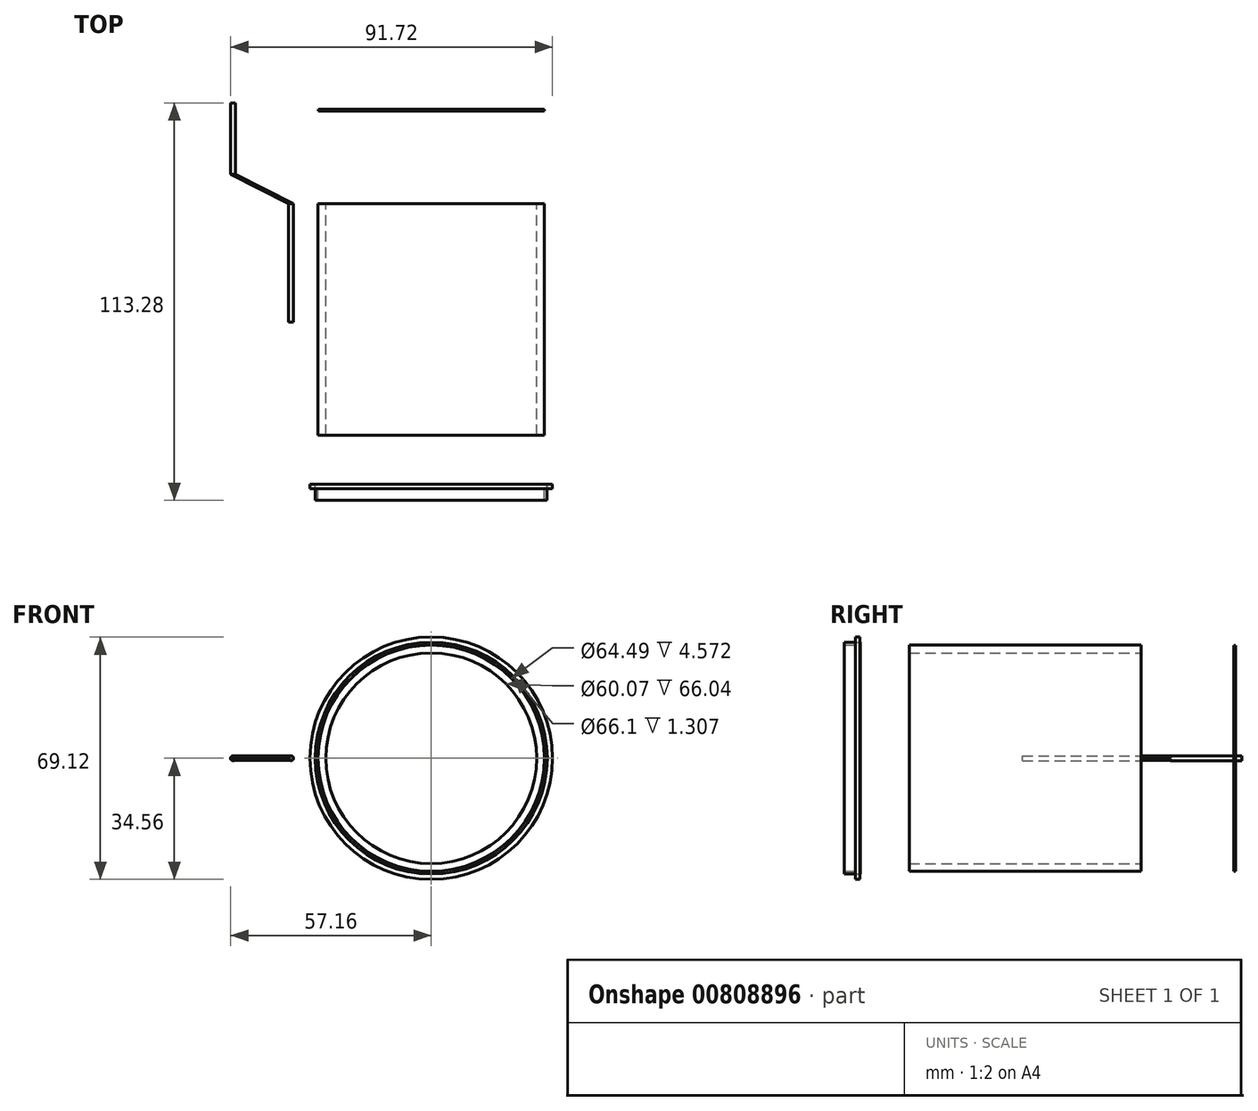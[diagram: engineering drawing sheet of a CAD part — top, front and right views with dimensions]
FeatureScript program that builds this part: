
annotation { "Feature Type Name" : "Feature", "Feature Type Description" : "" }
export const myFeature = defineFeature(function(context is Context, id is Id, definition is map)
    precondition{}
    {
        {
            var Q0;
            Q0=qCreatedBy(makeId("Front.planeOp"),FACE);
            var sketch = newSketch(context, id + "F0", { "sketchPlane" : qUnion([Q0])});
            skCircle(sketch, "E0", {"center": v(0, 0) * mm, "radius": 32.26 * mm});
            skCircle(sketch, "E1", {"center": v(0, 0) * mm, "radius": 30.03 * mm});
            skSolve(sketch);
        }
        {
            var Q0;
            Q0 = qSketchRegion(id + "F0", true);
            extrude(context, id + "F1", {"entities" : qUnion([Q0]), "depth" : 66.04 * mm, "offsetDistance" : 25.4 * mm});
        }
        {
            var Q0;
            Q0=qCreatedBy(makeId("Front.planeOp"),FACE);
            cPlane(context, id + "F2", {"entities" : qUnion([Q0]), "cplaneType" : CPlaneType.OFFSET, "offset" : 80 * mm, "width" : 152.4 * mm, "height" : 152.4 * mm});
        }
        {
            var Q0;
            Q0=qCreatedBy(id+"F2.planeOp",FACE);
            var sketch = newSketch(context, id + "F3", { "sketchPlane" : qUnion([Q0])});
            skCircle(sketch, "E2", {"center": v(0, 0) * mm, "radius": 33.02 * mm});
            skCircle(sketch, "E3", {"center": v(0, 0) * mm, "radius": 32.24 * mm});
            skSolve(sketch);
        }
        {
            var Q0;
            Q0=makeQuery(id+"F3.imprint","IMPRINT",FACE,{"disambiguationData":[TD([[makeQuery(id+"F3.imprint","IMPRINT",EDGE,{"derivedFrom":sQuery(id+"F3.wireOp",EDGE,"E2")}),1.0]])]});
            extrude(context, id + "F4", {"entities" : qUnion([Q0]), "depth" : 4.57 * mm, "offsetDistance" : 25.4 * mm});
        }
        {
            var Q0;
            Q0=qCreatedBy(makeId("Right.planeOp"),FACE);
            var sketch = newSketch(context, id + "F5", { "sketchPlane" : qUnion([Q0])});
            skLineSegment(sketch, "E4.bottom", {"start": v(-80.03, 33.05) * mm, "end": v(-81.33, 33.05) * mm});
            skLineSegment(sketch, "E4.top", {"start": v(-80.03, 34.56) * mm, "end": v(-81.33, 34.56) * mm});
            skLineSegment(sketch, "E4.left", {"start": v(-80.03, 33.05) * mm, "end": v(-80.03, 34.56) * mm});
            skLineSegment(sketch, "E4.right", {"start": v(-81.33, 33.05) * mm, "end": v(-81.33, 34.56) * mm});
            skSolve(sketch);
        }
        {
            var Q0;
            Q0=qCreatedBy(makeId("Top.planeOp"),FACE);
            var sketch = newSketch(context, id + "F6", { "sketchPlane" : qUnion([Q0])});
            skLineSegment(sketch, "E5.bottom", {"start": v(0, 0) * mm, "end": v(-52.45, 0) * mm});
            skLineSegment(sketch, "E5.top", {"start": v(0, -440.72) * mm, "end": v(-52.45, -440.72) * mm});
            skLineSegment(sketch, "E5.left", {"start": v(0, 0) * mm, "end": v(0, -440.72) * mm});
            skLineSegment(sketch, "E5.right", {"start": v(-52.45, 0) * mm, "end": v(-52.45, -440.72) * mm});
            skSolve(sketch);
        }
        {
            var Q0;
            Q0=makeQuery(id+"F5.imprint","IMPRINT",FACE,{"disambiguationData":[TD([[makeQuery(id+"F5.imprint","IMPRINT",EDGE,{"derivedFrom":sQuery(id+"F5.wireOp",EDGE,"E4.bottom")}),-1.0]])]});
            var Q1;
            Q1=sQuery(id+"F6.wireOp",EDGE,"E5.left");
            revolve(context, id + "F7", {"surfaceOperationType" : NewSurfaceOperationType.NEW, "entities" : qUnion([Q0]), "axis" : qUnion([Q1]), "revolveType" : RevolveType.FULL});
        }
        {
            var Q0;
            Q0=qCreatedBy(makeId("Front.planeOp"),FACE);
            cPlane(context, id + "F8", {"entities" : qUnion([Q0]), "cplaneType" : CPlaneType.OFFSET, "offset" : 26.92 * mm, "oppositeDirection" : true, "width" : 152.4 * mm, "height" : 152.4 * mm});
        }
        {
            var Q0;
            Q0=qCreatedBy(id+"F8.planeOp",FACE);
            var sketch = newSketch(context, id + "F9", { "sketchPlane" : qUnion([Q0])});
            skCircle(sketch, "E6", {"center": v(0, 0) * mm, "radius": 32.2 * mm});
            skSolve(sketch);
        }
        {
            var Q0;
            Q0 = qSketchRegion(id + "F9", true);
            extrude(context, id + "F10", {"entities" : qUnion([Q0]), "depth" : 0.48 * mm, "offsetDistance" : 25.4 * mm});
        }
        {
            var Q0;
            Q0=qCreatedBy(makeId("Front.planeOp"),FACE);
            var sketch = newSketch(context, id + "F11", { "sketchPlane" : qUnion([Q0])});
            skCircle(sketch, "E7", {"center": v(-39.93, 0) * mm, "radius": 0.68 * mm});
            skSolve(sketch);
        }
        {
            var Q0;
            Q0 = qSketchRegion(id + "F11", true);
            extrude(context, id + "F12", {"entities" : qUnion([Q0]), "depth" : 33.78 * mm, "offsetDistance" : 25.4 * mm});
        }
        {
            var Q0;
            Q0=qCreatedBy(makeId("Front.planeOp"),FACE);
            cPlane(context, id + "F13", {"entities" : qUnion([Q0]), "cplaneType" : CPlaneType.OFFSET, "offset" : 8.38 * mm, "oppositeDirection" : true, "width" : 152.4 * mm, "height" : 152.4 * mm});
        }
        {
            var Q0;
            Q0=qCreatedBy(id+"F13.planeOp",FACE);
            var sketch = newSketch(context, id + "F14", { "sketchPlane" : qUnion([Q0])});
            skCircle(sketch, "E8", {"center": v(-56.45, 0) * mm, "radius": 0.7 * mm});
            skSolve(sketch);
        }
        {
            var Q0;
            Q0 = qSketchRegion(id + "F14", true);
            extrude(context, id + "F15", {"entities" : qUnion([Q0]), "oppositeDirection" : true, "depth" : 20.32 * mm, "offsetDistance" : 25.4 * mm});
        }
        {
            var Q0;
            Q0=qCreatedBy(makeId("Top.planeOp"),FACE);
            var sketch = newSketch(context, id + "F16", { "sketchPlane" : qUnion([Q0])});
            skLineSegment(sketch, "E9", {"start": v(-55.76, 8.43) * mm, "end": v(-39.27, 0) * mm});
            skLineSegment(sketch, "E10", {"start": v(-40.63, 0) * mm, "end": v(-57.16, 8.4) * mm});
            skLineSegment(sketch, "E11", {"start": v(-55.76, 8.43) * mm, "end": v(-57.16, 8.4) * mm});
            skLineSegment(sketch, "E12", {"start": v(-40.63, 0) * mm, "end": v(-39.27, 0) * mm});
            skSolve(sketch);
        }
        {
            var Q0;
            Q0=makeQuery(id+"F16.imprint","IMPRINT",FACE,{"disambiguationData":[TD([[makeQuery(id+"F16.imprint","IMPRINT",EDGE,{"derivedFrom":sQuery(id+"F16.wireOp",EDGE,"E9")}),-1.0]])]});
            extrude(context, id + "F17", {"entities" : qUnion([Q0]), "depth" : 0.66 * mm, "offsetDistance" : 25.4 * mm});
        }
        {
            var Q0;
            Q0=makeQuery(id+"F17.opExtrude","CAP_FACE",FACE,{"disambiguationData":[OSD([sQuery(id+"F16.wireOp",EDGE,"E9"),sQuery(id+"F16.wireOp",EDGE,"E10"),sQuery(id+"F16.wireOp",EDGE,"E11"),sQuery(id+"F16.wireOp",EDGE,"E12")])],"isStart":true});
            extrude(context, id + "F18", {"entities" : qUnion([Q0]), "depth" : 0.69 * mm, "offsetDistance" : 25.4 * mm});
        }
        {
            var Q0;
            Q0=makeQuery(id+"F18.opExtrude","CAP_EDGE",EDGE,{"disambiguationData":[OSD([sQuery(id+"F16.wireOp",EDGE,"E9")])],"isStart":false});
            var Q1;
            Q1=makeQuery(id+"F17.opExtrude","CAP_EDGE",EDGE,{"disambiguationData":[OSD([sQuery(id+"F16.wireOp",EDGE,"E9")])],"isStart":false});
            var Q2;
            Q2=makeQuery(id+"F18.opExtrude","CAP_EDGE",EDGE,{"disambiguationData":[OSD([sQuery(id+"F16.wireOp",EDGE,"E10")])],"isStart":false});
            var Q3;
            Q3=makeQuery(id+"F17.opExtrude","CAP_EDGE",EDGE,{"disambiguationData":[OSD([sQuery(id+"F16.wireOp",EDGE,"E10")])],"isStart":false});
            fillet(context, id + "F19", {"entities" : qUnion([Q0, Q1, Q2, Q3]), "radius" : 0.5 * mm, "tangentPropagation" : true, "allowEdgeOverflow" : false});
        }
    });
